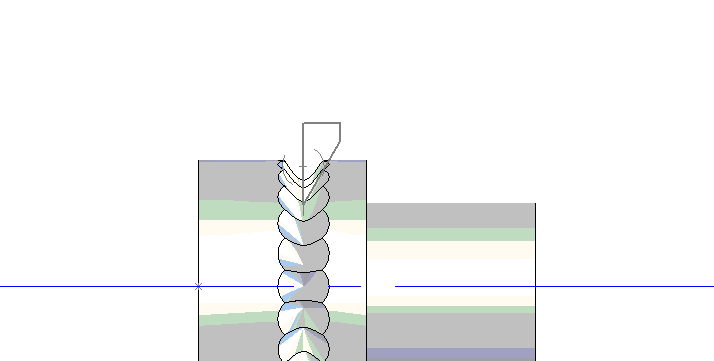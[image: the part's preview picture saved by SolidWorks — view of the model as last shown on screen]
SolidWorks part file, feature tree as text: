
SOLIDWORKS PART (.sldprt)
format: sldprt  version: not decoded by parser v0  size: 371,200 bytes
history: native  units: mm
features: sketch x2, revolve x1, cut_revolve x1, pattern_circular x1 (+11 scaffold rows collapsed)
feature tree (16):
  scaffold x11  (default folders/planes/origin — collapsed)
  sketch  "Sketch1"  dims[D1=2.0066mm D2=3.175mm D3=6.35mm D4=6.35mm D5=4.7625mm]
  revolve  "Revolve1"  Angle=360deg
  sketch  "Sketch3"  dims[c1.D2=1.5875mm c1.D6=1.5875mm c1.D1=3.175mm c1.D3=2.7686mm c1.D4=1.5875mm c1.D5=~0.939273mm c2.D5=~122.32075deg c3.D5=~2.08969mm c4.D5=30.0deg c4.D4=1.0668mm c4.D6=0.7112mm c5.D4=0.254mm c5.D1=2.3876mm]
  cut_revolve  "Cut-Revolve2"  Angle=360deg
  pattern_circular  "CirPattern1"  Count=24 Angle=15deg
decode coverage: 5 of 5 modeling features carry decoded parameters
note: ~ marks probable driven/reference dimensions
note: suppression state not decoded; provenance and decode notes live in map.json
